# Revit family: FP-Revit20-en-RF178ANUX1-RefrigeratorFreezer-90004898A-US-CA
name_source: partatom
category: Specialty Equipment
units: mm (PartAtom-declared; Revit-internal decimal feet)

## family parameters
Always vertical = Yes
Cut with Voids When Loaded = Yes
Part Type = Normal
Room Calculation Point = No
Round Connector Dimension = Use Diameter
Shared = No
Work Plane-Based = No

## types (2) — shared parameters
Chassis = Fisher & Paykel - Aluminium
Clearance = Fisher & Paykel - Clearance Required (Non-Combustible)
Clearance - Vent = Fisher & Paykel - Clearance Required (Non-Combustible)
Clearance Cavity = Yes
Description = French Door Refrigerator Freezer with Water and Ice
Door swing = Yes
Electrical Specifications = Supply: 220V - 240V, 50Hz, Service: 10A circuit
Handle finish = Fisher & Paykel - Grey, Charcoal
Left side clearance = 20 mm  [stored 0.0656168 ft]
Manufacturer = Fisher & Paykel
Plumbing Specifications = Water Supply: 1/4" LLDPE piping, Pressure: Max 827 kPa (120 psi) @ 68°F (20°C)
Product depth = 707 mm
Product height = 1725 mm  [stored 5.65945 ft]
Product width = 790 mm  [stored 2.59186 ft]
Rear clearance = 30 mm  [stored 0.0984252 ft]
Right side clearance = 20 mm  [stored 0.0656168 ft]
Top vent clearance = 50 mm  [stored 0.164042 ft]
URL = www.fisherpaykel.com
Vent clearance (see planning guide for options) = Yes
Water Dispenser material = Fisher & Paykel - Black, Matte
zero-valued in all types: Default Elevation

## type names (no varying parameters)
- RF505ANUX1
- RF178ANUX1

note: column(s) folded — value = type name in every type: Model

note: [stored X ft] marks values corroborated as IEEE doubles in the binary element streams (Revit-internal decimal feet)

## geometry (parser evidence)
native form markers: Sweep x16
no freeform markers — native parametric forms only
